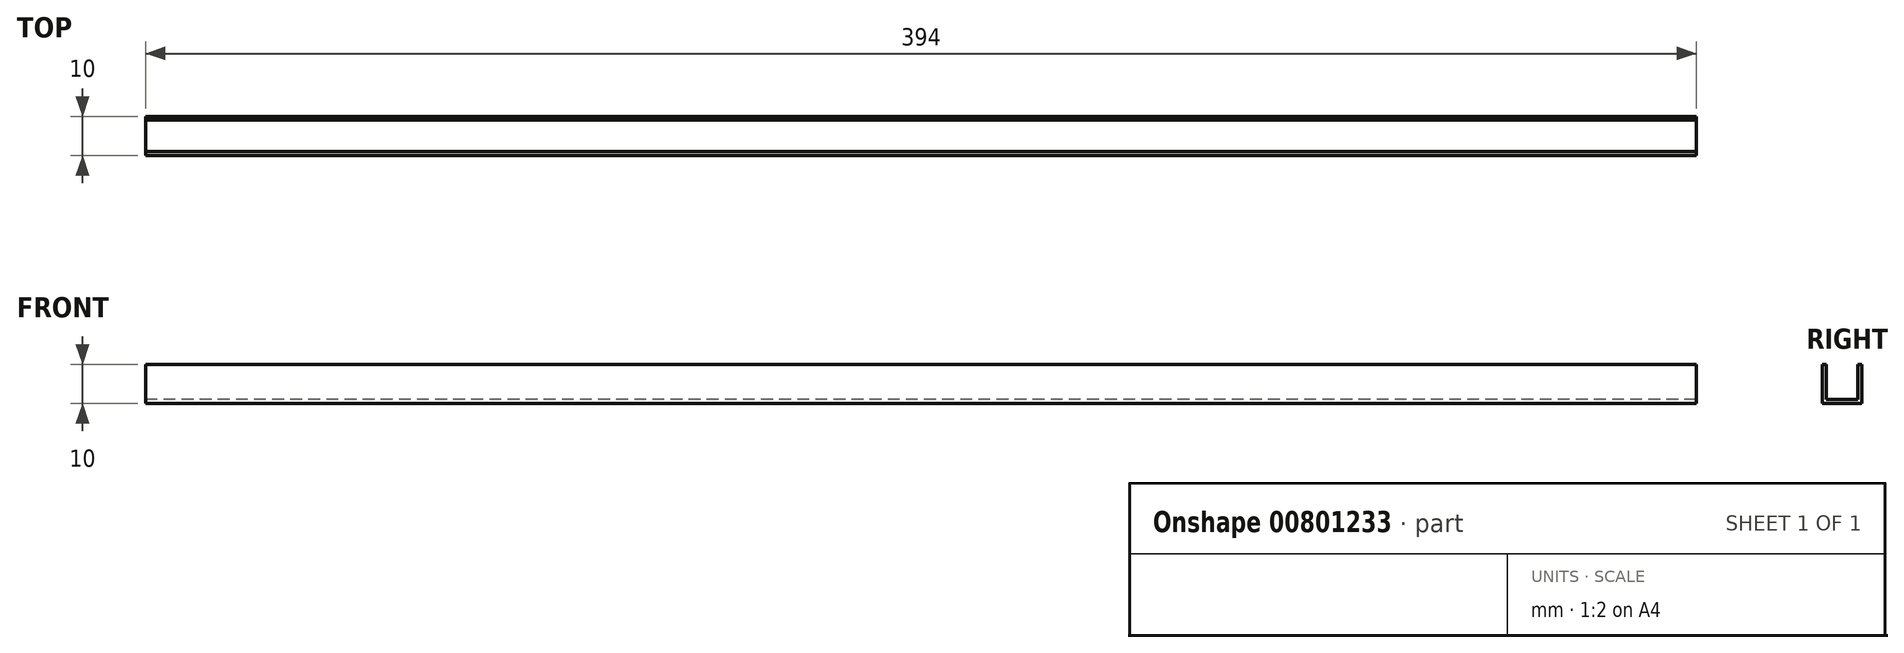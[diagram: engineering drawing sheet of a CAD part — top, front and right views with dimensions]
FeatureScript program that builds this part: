
annotation { "Feature Type Name" : "Feature", "Feature Type Description" : "" }
export const myFeature = defineFeature(function(context is Context, id is Id, definition is map)
    precondition{}
    {
        {
            var Q0;
            Q0=qCreatedBy(makeId("Right.planeOp"),FACE);
            var sketch = newSketch(context, id + "F0", { "sketchPlane" : qUnion([Q0])});
            skLineSegment(sketch, "E0.bottom", {"start": v(-5, 5) * mm, "end": v(-4, 5) * mm});
            skLineSegment(sketch, "E0.top", {"start": v(-5, -5) * mm, "end": v(5, -5) * mm});
            skLineSegment(sketch, "E0.left", {"start": v(-5, 5) * mm, "end": v(-5, -5) * mm});
            skLineSegment(sketch, "E0.right", {"start": v(5, 5) * mm, "end": v(5, -5) * mm});
            skPoint(sketch, "E0.middle", {"position": v(0, 0) * mm});
            skLineSegment(sketch, "E1.0", {"start": v(4, 5) * mm, "end": v(4, -4) * mm});
            skLineSegment(sketch, "E1.2", {"start": v(-4, 5) * mm, "end": v(-4, -4) * mm});
            skLineSegment(sketch, "E1.3", {"start": v(-4, -4) * mm, "end": v(4, -4) * mm});
            skLineSegment(sketch, "E2.trimOffspring", {"start": v(4, 5) * mm, "end": v(5, 5) * mm});
            skSolve(sketch);
        }
        {
            var Q0;
            Q0=makeQuery(id+"F0.imprint","IMPRINT",FACE,{"disambiguationData":[TD([[makeQuery(id+"F0.imprint","IMPRINT",EDGE,{"derivedFrom":sQuery(id+"F0.wireOp",EDGE,"E0.bottom")}),-1.0]])]});
            extrude(context, id + "F1", {"entities" : qUnion([Q0]), "depth" : (400 - 6) * mm, "offsetDistance" : 25 * mm, "symmetric" : true});
        }
    });
